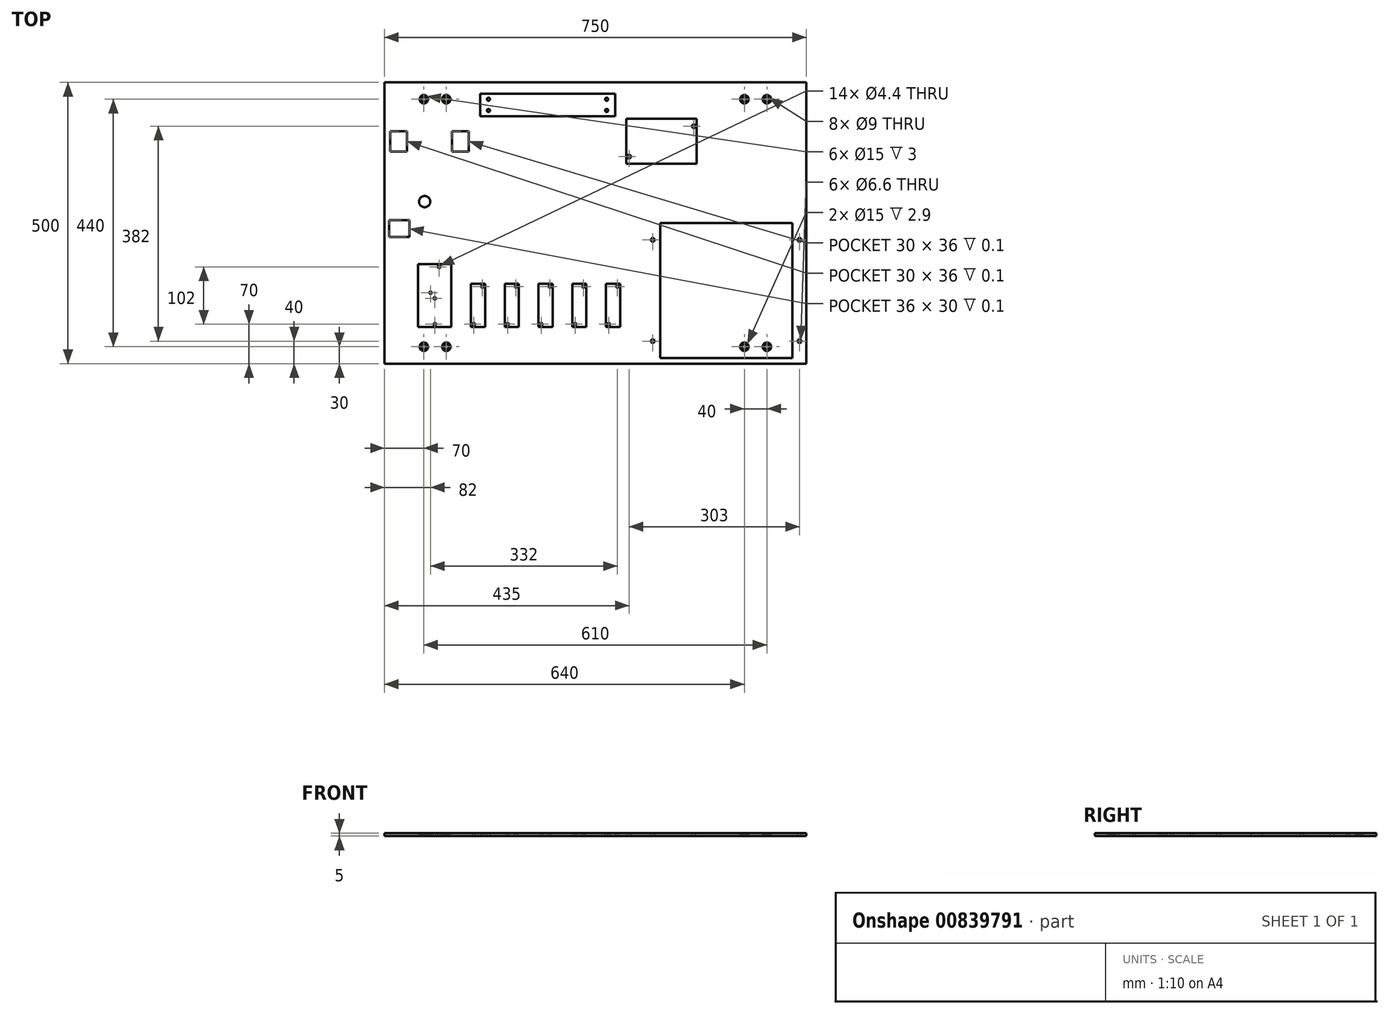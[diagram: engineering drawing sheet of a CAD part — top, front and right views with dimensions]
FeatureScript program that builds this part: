
annotation { "Feature Type Name" : "Feature", "Feature Type Description" : "" }
export const myFeature = defineFeature(function(context is Context, id is Id, definition is map)
    precondition{}
    {
        {
            var Q0;
            Q0=qCreatedBy(makeId("Top.planeOp"),FACE);
            var sketch = newSketch(context, id + "F0", { "sketchPlane" : qUnion([Q0])});
            skLineSegment(sketch, "E0.bottom", {"start": v(-375, 250) * mm, "end": v(375, 250) * mm});
            skLineSegment(sketch, "E0.top", {"start": v(-375, -250) * mm, "end": v(375, -250) * mm});
            skLineSegment(sketch, "E0.left", {"start": v(-375, 250) * mm, "end": v(-375, -250) * mm});
            skLineSegment(sketch, "E0.right", {"start": v(375, 250) * mm, "end": v(375, -250) * mm});
            skPoint(sketch, "E0.middle", {"position": v(0, 0) * mm});
            skSolve(sketch);
        }
        {
            var Q0;
            Q0=makeQuery(id+"F0.imprint","IMPRINT",FACE,{"disambiguationData":[TD([[makeQuery(id+"F0.imprint","IMPRINT",EDGE,{"derivedFrom":sQuery(id+"F0.wireOp",EDGE,"4meduJy7-bVkd-hp0T-bakh-5B8NUv365NF5")}),1.0]])]});
            var Q1;
            Q1=makeQuery(id+"F0.imprint","IMPRINT",FACE,{"disambiguationData":[TD([[makeQuery(id+"F0.imprint","IMPRINT",EDGE,{"derivedFrom":sQuery(id+"F0.wireOp",EDGE,"E0.bottom")}),-1.0]])]});
            var Q2;
            Q2=makeQuery(id+"F0.imprint","IMPRINT",FACE,{"disambiguationData":[TD([[makeQuery(id+"F0.imprint","IMPRINT",EDGE,{"derivedFrom":sQuery(id+"F0.wireOp",EDGE,"ac5e37f8-856c-49cc-b007-1c18f545f4330.MirrorC")}),-1.0]])]});
            var Q3;
            Q3=makeQuery(id+"F0.imprint","IMPRINT",FACE,{"disambiguationData":[TD([[makeQuery(id+"F0.imprint","IMPRINT",EDGE,{"derivedFrom":sQuery(id+"F0.wireOp",EDGE,"55b44df1-bd7d-4fb0-bc28-21b46cb8f5820.MirrorC")}),1.0]])]});
            var Q4;
            Q4=makeQuery(id+"F0.imprint","IMPRINT",FACE,{"disambiguationData":[TD([[makeQuery(id+"F0.imprint","IMPRINT",EDGE,{"derivedFrom":sQuery(id+"F0.wireOp",EDGE,"ec86db50-ea34-4b74-b64d-a008dce2ac710.MirrorC")}),-1.0]])]});
            var Q5;
            Q5=makeQuery(id+"F0.imprint","IMPRINT",FACE,{"disambiguationData":[TD([[makeQuery(id+"F0.imprint","IMPRINT",EDGE,{"derivedFrom":sQuery(id+"F0.wireOp",EDGE,"bd3b83fc-f496-4a5d-aeb5-383bc6339bfd0.MirrorC")}),1.0]])]});
            var Q6;
            Q6=makeQuery(id+"F0.imprint","IMPRINT",FACE,{"disambiguationData":[TD([[makeQuery(id+"F0.imprint","IMPRINT",EDGE,{"derivedFrom":sQuery(id+"F0.wireOp",EDGE,"f239e742-8900-48a1-b46c-c08f9f2a8f400.MirrorC")}),-1.0]])]});
            var Q7;
            Q7=makeQuery(id+"F0.imprint","IMPRINT",FACE,{"disambiguationData":[TD([[makeQuery(id+"F0.imprint","IMPRINT",EDGE,{"derivedFrom":sQuery(id+"F0.wireOp",EDGE,"240437df-a570-4469-8774-de0f0eec39ff0.MirrorC")}),-1.0]])]});
            var Q8;
            Q8=makeQuery(id+"F0.imprint","IMPRINT",FACE,{"disambiguationData":[TD([[makeQuery(id+"F0.imprint","IMPRINT",EDGE,{"derivedFrom":sQuery(id+"F0.wireOp",EDGE,"720a3da4-655f-46b3-9474-92b0fe536cc30.MirrorC")}),1.0]])]});
            extrude(context, id + "F1", {"entities" : qUnion([Q0, Q1, Q2, Q3, Q4, Q5, Q6, Q7, Q8]), "depth" : 5 * mm, "offsetDistance" : 25 * mm});
        }
        {
            var Q0;
            Q0=makeQuery(id+"F1.opExtrude","CAP_FACE",FACE,{"disambiguationData":[OSD([sQuery(id+"F0.wireOp",EDGE,"E0.bottom"),sQuery(id+"F0.wireOp",EDGE,"E0.top"),sQuery(id+"F0.wireOp",EDGE,"E0.left"),sQuery(id+"F0.wireOp",EDGE,"E0.right")])],"isStart":false});
            var sketch = newSketch(context, id + "F2", { "sketchPlane" : qUnion([Q0])});
            skPoint(sketch, "E1", {"position": v(-305, 220) * mm});
            skPoint(sketch, "E2", {"position": v(-265, 220) * mm});
            skPoint(sketch, "E3", {"position": v(265, 220) * mm});
            skPoint(sketch, "E4", {"position": v(305, 220) * mm});
            skPoint(sketch, "E5", {"position": v(-305, -220) * mm});
            skPoint(sketch, "E6", {"position": v(-265, -220) * mm});
            skPoint(sketch, "E7", {"position": v(265, -220) * mm});
            skPoint(sketch, "E8", {"position": v(305, -220) * mm});
            skSolve(sketch);
        }
        {
            var Q0;
            Q0=makeQuery(id+"F1.opExtrude","CAP_FACE",FACE,{"disambiguationData":[OSD([sQuery(id+"F0.wireOp",EDGE,"E0.bottom"),sQuery(id+"F0.wireOp",EDGE,"E0.top"),sQuery(id+"F0.wireOp",EDGE,"E0.left"),sQuery(id+"F0.wireOp",EDGE,"E0.right")])],"isStart":false});
            var sketch = newSketch(context, id + "F3", { "sketchPlane" : qUnion([Q0])});
            skLineSegment(sketch, "E9.bottom", {"start": v(115, 0) * mm, "end": v(350, 0) * mm});
            skLineSegment(sketch, "E9.top", {"start": v(115, -240) * mm, "end": v(350, -240) * mm});
            skLineSegment(sketch, "E9.left", {"start": v(115, 0) * mm, "end": v(115, -240) * mm});
            skLineSegment(sketch, "E9.right", {"start": v(350, 0) * mm, "end": v(350, -240) * mm});
            skLineSegment(sketch, "E10.bottom", {"start": v(-256, -185) * mm, "end": v(-315, -185) * mm});
            skLineSegment(sketch, "E10.top", {"start": v(-256, -73) * mm, "end": v(-315, -73) * mm});
            skLineSegment(sketch, "E10.left", {"start": v(-256, -185) * mm, "end": v(-256, -73) * mm});
            skLineSegment(sketch, "E10.right", {"start": v(-315, -185) * mm, "end": v(-315, -73) * mm});
            skLineSegment(sketch, "E11.bottom", {"start": v(-16, -108) * mm, "end": v(-41, -108) * mm});
            skLineSegment(sketch, "E11.top", {"start": v(-16, -185) * mm, "end": v(-41, -185) * mm});
            skLineSegment(sketch, "E11.left", {"start": v(-16, -108) * mm, "end": v(-16, -185) * mm});
            skLineSegment(sketch, "E11.right", {"start": v(-41, -108) * mm, "end": v(-41, -185) * mm});
            skLineSegment(sketch, "E12.bottom", {"start": v(-76, -108) * mm, "end": v(-101, -108) * mm});
            skLineSegment(sketch, "E12.top", {"start": v(-76, -185) * mm, "end": v(-101, -185) * mm});
            skLineSegment(sketch, "E12.left", {"start": v(-76, -108) * mm, "end": v(-76, -185) * mm});
            skLineSegment(sketch, "E12.right", {"start": v(-101, -108) * mm, "end": v(-101, -185) * mm});
            skLineSegment(sketch, "E13.bottom", {"start": v(-136, -108) * mm, "end": v(-161, -108) * mm});
            skLineSegment(sketch, "E13.top", {"start": v(-136, -185) * mm, "end": v(-161, -185) * mm});
            skLineSegment(sketch, "E13.left", {"start": v(-136, -108) * mm, "end": v(-136, -185) * mm});
            skLineSegment(sketch, "E13.right", {"start": v(-161, -108) * mm, "end": v(-161, -185) * mm});
            skLineSegment(sketch, "E14.bottom", {"start": v(-221, -108) * mm, "end": v(-196, -108) * mm});
            skLineSegment(sketch, "E14.top", {"start": v(-221, -185) * mm, "end": v(-196, -185) * mm});
            skLineSegment(sketch, "E14.left", {"start": v(-221, -108) * mm, "end": v(-221, -185) * mm});
            skLineSegment(sketch, "E14.right", {"start": v(-196, -108) * mm, "end": v(-196, -185) * mm});
            skLineSegment(sketch, "E15", {"start": v(-285, -50) * mm, "end": v(-285, 100) * mm});
            skLineSegment(sketch, "E16", {"start": v(-285, 100) * mm, "end": v(32, 100) * mm});
            skLineSegment(sketch, "E17.bottom", {"start": v(-205, 230) * mm, "end": v(35, 230) * mm});
            skLineSegment(sketch, "E17.top", {"start": v(-205, 190) * mm, "end": v(35, 190) * mm});
            skLineSegment(sketch, "E17.left", {"start": v(-205, 230) * mm, "end": v(-205, 190) * mm});
            skLineSegment(sketch, "E17.right", {"start": v(35, 230) * mm, "end": v(35, 190) * mm});
            skLineSegment(sketch, "E18.bottom", {"start": v(-324.13, 116.04) * mm, "end": v(-266.88, 116.04) * mm});
            skLineSegment(sketch, "E18.top", {"start": v(-324.13, 173.96) * mm, "end": v(-266.88, 173.96) * mm});
            skLineSegment(sketch, "E18.left", {"start": v(-324.13, 173.96) * mm, "end": v(-324.13, 116.04) * mm});
            skLineSegment(sketch, "E18.right", {"start": v(-266.88, 173.96) * mm, "end": v(-266.88, 116.04) * mm});
            skLineSegment(sketch, "E19", {"start": v(195, 210) * mm, "end": v(35, 210) * mm});
            skLineSegment(sketch, "E20", {"start": v(195, 210) * mm, "end": v(195, 165) * mm});
            skLineSegment(sketch, "E21", {"start": v(55, 145) * mm, "end": v(-266.88, 145) * mm});
            skPoint(sketch, "E22.1.internal.snap0", {"position": v(-285.5, -73) * mm});
            skPoint(sketch, "E23.2.internal.snap0", {"position": v(-208.5, -108) * mm});
            skPoint(sketch, "E24.1.internal.snap0", {"position": v(-148.5, -108) * mm});
            skLineSegment(sketch, "E25", {"start": v(-324.13, 145) * mm, "end": v(-363.07, 145) * mm});
            skLineSegment(sketch, "E26.bottom", {"start": v(55, 185) * mm, "end": v(180, 185) * mm});
            skLineSegment(sketch, "E26.top", {"start": v(55, 105) * mm, "end": v(180, 105) * mm});
            skLineSegment(sketch, "E26.left", {"start": v(55, 185) * mm, "end": v(55, 105) * mm});
            skLineSegment(sketch, "E26.right", {"start": v(180, 185) * mm, "end": v(180, 105) * mm});
            skPoint(sketch, "E27", {"position": v(55, 145) * mm});
            skLineSegment(sketch, "E28.left", {"start": v(210, 165) * mm, "end": v(210, 122.2) * mm});
            skPoint(sketch, "E28.middle", {"position": v(180, 145) * mm});
            skLineSegment(sketch, "E29", {"start": v(210, 122.2) * mm, "end": v(180, 122.2) * mm});
            skLineSegment(sketch, "E30", {"start": v(210, 165) * mm, "end": v(180, 165) * mm});
            skLineSegment(sketch, "E31", {"start": v(210, 143.6) * mm, "end": v(375, 143.6) * mm});
            skPoint(sketch, "E32", {"position": v(195, 165) * mm});
            skPoint(sketch, "E33", {"position": v(195, 122.2) * mm});
            skLineSegment(sketch, "E34", {"start": v(195, 100) * mm, "end": v(195, 122.2) * mm});
            skLineSegment(sketch, "E35", {"start": v(195, 30.37) * mm, "end": v(195, 100) * mm});
            skPoint(sketch, "E36", {"position": v(-295.5, 116.04) * mm});
            skLineSegment(sketch, "E37", {"start": v(-285, 100) * mm, "end": v(-295.5, 100) * mm});
            skLineSegment(sketch, "E38", {"start": v(-295.5, 100) * mm, "end": v(-295.5, 116.04) * mm});
            skLineSegment(sketch, "E39.bottom", {"start": v(19, -108) * mm, "end": v(44, -108) * mm});
            skLineSegment(sketch, "E39.top", {"start": v(19, -185) * mm, "end": v(44, -185) * mm});
            skLineSegment(sketch, "E39.left", {"start": v(19, -108) * mm, "end": v(19, -185) * mm});
            skLineSegment(sketch, "E39.right", {"start": v(44, -108) * mm, "end": v(44, -185) * mm});
            skLineSegment(sketch, "E40", {"start": v(-208.5, -108) * mm, "end": v(-208.5, -48) * mm});
            skLineSegment(sketch, "E41", {"start": v(-148.5, -108) * mm, "end": v(-148.5, 11.13) * mm});
            skLineSegment(sketch, "E42", {"start": v(-88.5, -108) * mm, "end": v(-88.5, 9.17) * mm});
            skLineSegment(sketch, "E43", {"start": v(-28.5, -108) * mm, "end": v(-28.5, -46.89) * mm});
            skLineSegment(sketch, "E44", {"start": v(31.5, -108) * mm, "end": v(31.5, 13.08) * mm});
            skSolve(sketch);
        }
        {
            var Q0;
            Q0=sQuery(id+"F2.wireOp",VERTEX,"E1");
            var Q1;
            Q1=sQuery(id+"F2.wireOp",VERTEX,"E2");
            var Q2;
            Q2=sQuery(id+"F2.wireOp",VERTEX,"E5");
            var Q3;
            Q3=sQuery(id+"F2.wireOp",VERTEX,"E6");
            var Q4;
            Q4=sQuery(id+"F2.wireOp",VERTEX,"E7");
            var Q5;
            Q5=sQuery(id+"F2.wireOp",VERTEX,"E8");
            var Q6;
            Q6=sQuery(id+"F2.wireOp",VERTEX,"E3");
            var Q7;
            Q7=sQuery(id+"F2.wireOp",VERTEX,"E4");
            var Q8;
            Q8=makeQuery(id+"F1.opExtrude","SWEPT_BODY",BODY,{"disambiguationData":[OSD([sQuery(id+"F0.wireOp",EDGE,"E0.bottom"),sQuery(id+"F0.wireOp",EDGE,"E0.top"),sQuery(id+"F0.wireOp",EDGE,"E0.left"),sQuery(id+"F0.wireOp",EDGE,"E0.right")])]});
            hole(context, id + "F4", {"style" : HoleStyle.C_BORE, "endStyle" : HoleEndStyle.THROUGH, "holeDiameter" : 9 * mm, "cBoreDiameter" : 15 * mm, "cBoreDepth" : 3 * mm, "majorDiameter" : 5 * mm, "isTappedThrough" : true, "tappedDepth" : 12 * mm, "tapClearance" : 3, "locations" : qUnion([Q0, Q1, Q2, Q3, Q4, Q5, Q6, Q7]), "scope" : qUnion([Q8])});
        }
        {
            var Q0;
            Q0=makeQuery(id+"F3.imprint","IMPRINT",FACE,{"disambiguationData":[TD([[makeQuery(id+"F3.imprint","IMPRINT",EDGE,{"derivedFrom":sQuery(id+"F3.wireOp",EDGE,"E9.bottom")}),-1.0]])]});
            extrude(context, id + "F5", {"entities" : qUnion([Q0]), "operationType" : NewBodyOperationType.REMOVE, "oppositeDirection" : true, "depth" : 0.1 * mm, "offsetDistance" : 25 * mm});
        }
        {
            var Q0;
            {var subQ3=sQuery(id+"F3.wireOp",EDGE,"E26.bottom");Q0=makeQuery(id+"F3.imprint","IMPRINT",FACE,{"disambiguationData":[TD([[makeQuery(id+"F3.imprint","IMPRINT",EDGE,{"derivedFrom":subQ3}),-1.0]])]});}
            extrude(context, id + "F6", {"entities" : qUnion([Q0]), "operationType" : NewBodyOperationType.REMOVE, "oppositeDirection" : true, "depth" : 0.1 * mm, "offsetDistance" : 25 * mm});
        }
        {
            var Q0;
            Q0=makeQuery(id+"F3.imprint","IMPRINT",FACE,{"disambiguationData":[TD([[makeQuery(id+"F3.imprint","IMPRINT",EDGE,{"derivedFrom":sQuery(id+"F3.wireOp",EDGE,"E10.bottom")}),-1.0]])]});
            extrude(context, id + "F7", {"entities" : qUnion([Q0]), "operationType" : NewBodyOperationType.REMOVE, "oppositeDirection" : true, "depth" : 0.1 * mm, "offsetDistance" : 25 * mm});
        }
        {
            var Q0;
            {var subQ1=sQuery(id+"F3.wireOp",EDGE,"E17.bottom");Q0=makeQuery(id+"F3.imprint","IMPRINT",FACE,{"disambiguationData":[TD([[makeQuery(id+"F3.imprint","IMPRINT",EDGE,{"derivedFrom":subQ1}),-1.0]])]});}
            extrude(context, id + "F8", {"entities" : qUnion([Q0]), "operationType" : NewBodyOperationType.REMOVE, "oppositeDirection" : true, "depth" : 0.1 * mm, "offsetDistance" : 25 * mm});
        }
        {
            var Q0;
            Q0=makeQuery(id+"F3.imprint","IMPRINT",FACE,{"disambiguationData":[TD([[makeQuery(id+"F3.imprint","IMPRINT",EDGE,{"derivedFrom":sQuery(id+"F3.wireOp",EDGE,"E14.top")}),1.0]])]});
            var Q1;
            Q1=makeQuery(id+"F3.imprint","IMPRINT",FACE,{"disambiguationData":[TD([[makeQuery(id+"F3.imprint","IMPRINT",EDGE,{"derivedFrom":sQuery(id+"F3.wireOp",EDGE,"E13.top")}),-1.0]])]});
            var Q2;
            Q2=makeQuery(id+"F3.imprint","IMPRINT",FACE,{"disambiguationData":[TD([[makeQuery(id+"F3.imprint","IMPRINT",EDGE,{"derivedFrom":sQuery(id+"F3.wireOp",EDGE,"E12.top")}),-1.0]])]});
            var Q3;
            Q3=makeQuery(id+"F3.imprint","IMPRINT",FACE,{"disambiguationData":[TD([[makeQuery(id+"F3.imprint","IMPRINT",EDGE,{"derivedFrom":sQuery(id+"F3.wireOp",EDGE,"E11.top")}),-1.0]])]});
            var Q4;
            Q4=makeQuery(id+"F3.imprint","IMPRINT",FACE,{"disambiguationData":[TD([[makeQuery(id+"F3.imprint","IMPRINT",EDGE,{"derivedFrom":sQuery(id+"F3.wireOp",EDGE,"E39.bottom")}),-1.0]])]});
            extrude(context, id + "F9", {"entities" : qUnion([Q0, Q1, Q2, Q3, Q4]), "operationType" : NewBodyOperationType.REMOVE, "oppositeDirection" : true, "depth" : 0.1 * mm, "offsetDistance" : 25 * mm});
        }
        {
            var Q0;
            Q0=makeQuery(id+"F1.opExtrude","CAP_FACE",FACE,{"disambiguationData":[OSD([sQuery(id+"F0.wireOp",EDGE,"E0.bottom"),sQuery(id+"F0.wireOp",EDGE,"E0.top"),sQuery(id+"F0.wireOp",EDGE,"E0.left"),sQuery(id+"F0.wireOp",EDGE,"E0.right")])],"isStart":false});
            var sketch = newSketch(context, id + "F10", { "sketchPlane" : qUnion([Q0])});
            skPoint(sketch, "E45", {"position": v(-201, -113) * mm});
            skPoint(sketch, "E46", {"position": v(-216, -180) * mm});
            skPoint(sketch, "E47", {"position": v(-278, -78) * mm});
            skPoint(sketch, "E48", {"position": v(-293, -124) * mm});
            skPoint(sketch, "E49", {"position": v(-285.5, -134) * mm});
            skPoint(sketch, "E50", {"position": v(-285.5, -180) * mm});
            skPoint(sketch, "E51", {"position": v(-141, -113) * mm});
            skPoint(sketch, "E52", {"position": v(-156, -180) * mm});
            skPoint(sketch, "E53", {"position": v(-96, -180) * mm});
            skPoint(sketch, "E54", {"position": v(-81, -113) * mm});
            skPoint(sketch, "E55", {"position": v(-21, -113) * mm});
            skPoint(sketch, "E56", {"position": v(-36, -180) * mm});
            skPoint(sketch, "E57", {"position": v(24, -180) * mm});
            skPoint(sketch, "E58", {"position": v(39, -113) * mm});
            skPoint(sketch, "E59", {"position": v(-190, 220) * mm});
            skLineSegment(sketch, "E60", {"start": v(-205, 210) * mm, "end": v(35, 210) * mm, "construction": true});
            skLineSegment(sketch, "E61", {"start": v(-85, 190) * mm, "end": v(-85, 230) * mm, "construction": true});
            skPoint(sketch, "E62.MirrorP", {"position": v(-190, 200) * mm});
            skPoint(sketch, "E63.MirrorP", {"position": v(20, 220) * mm});
            skPoint(sketch, "E64.MirrorP", {"position": v(20, 200) * mm});
            skPoint(sketch, "E65", {"position": v(60, 118) * mm});
            skPoint(sketch, "E66", {"position": v(175, 172) * mm});
            skPoint(sketch, "E67", {"position": v(102, -30) * mm});
            skLineSegment(sketch, "E68", {"start": v(232.5, 0) * mm, "end": v(232.5, -240) * mm, "construction": true});
            skLineSegment(sketch, "E69", {"start": v(115, -120) * mm, "end": v(350, -120) * mm, "construction": true});
            skPoint(sketch, "E70.MirrorP", {"position": v(363, -30) * mm});
            skPoint(sketch, "E71.MirrorP", {"position": v(102, -210) * mm});
            skPoint(sketch, "E72.MirrorP", {"position": v(363, -210) * mm});
            skSolve(sketch);
        }
        {
            var Q0;
            Q0=sQuery(id+"F10.wireOp",VERTEX,"E49");
            var Q1;
            Q1=sQuery(id+"F10.wireOp",VERTEX,"E48");
            var Q2;
            Q2=sQuery(id+"F10.wireOp",VERTEX,"E47");
            var Q3;
            Q3=sQuery(id+"F10.wireOp",VERTEX,"E50");
            var Q4;
            Q4=sQuery(id+"F10.wireOp",VERTEX,"E46");
            var Q5;
            Q5=sQuery(id+"F10.wireOp",VERTEX,"E45");
            var Q6;
            Q6=sQuery(id+"F10.wireOp",VERTEX,"E51");
            var Q7;
            Q7=sQuery(id+"F10.wireOp",VERTEX,"E52");
            var Q8;
            Q8=sQuery(id+"F10.wireOp",VERTEX,"E53");
            var Q9;
            Q9=sQuery(id+"F10.wireOp",VERTEX,"E54");
            var Q10;
            Q10=sQuery(id+"F10.wireOp",VERTEX,"E55");
            var Q11;
            Q11=sQuery(id+"F10.wireOp",VERTEX,"E56");
            var Q12;
            Q12=sQuery(id+"F10.wireOp",VERTEX,"E57");
            var Q13;
            Q13=sQuery(id+"F10.wireOp",VERTEX,"E58");
            var Q14;
            Q14=makeQuery(id+"F1.opExtrude","SWEPT_BODY",BODY,{"disambiguationData":[OSD([sQuery(id+"F0.wireOp",EDGE,"E0.bottom"),sQuery(id+"F0.wireOp",EDGE,"E0.top"),sQuery(id+"F0.wireOp",EDGE,"E0.left"),sQuery(id+"F0.wireOp",EDGE,"E0.right")])]});
            hole(context, id + "F11", {"style" : HoleStyle.SIMPLE, "endStyle" : HoleEndStyle.THROUGH, "standardTappedOrClearance" : lookupTablePath({ "fit" : "Normal", "standard" : "ISO", "size" : "M4", "type" : "Clearance" }), "standardBlindInLast" : lookupTablePath({ "fit" : "Standard", "standard" : "ISO", "size" : "M4", "type" : "Clearance" }), "holeDiameter" : 4.4 * mm, "majorDiameter" : 5 * mm, "isTappedThrough" : true, "tappedDepth" : 12 * mm, "tapClearance" : 3, "locations" : qUnion([Q0, Q1, Q2, Q3, Q4, Q5, Q6, Q7, Q8, Q9, Q10, Q11, Q12, Q13]), "scope" : qUnion([Q14])});
        }
        {
            var Q0;
            Q0=sQuery(id+"F10.wireOp",VERTEX,"E59");
            var Q1;
            Q1=sQuery(id+"F10.wireOp",VERTEX,"E62.MirrorP");
            var Q2;
            Q2=sQuery(id+"F10.wireOp",VERTEX,"E64.MirrorP");
            var Q3;
            Q3=sQuery(id+"F10.wireOp",VERTEX,"E63.MirrorP");
            var Q4;
            Q4=makeQuery(id+"F1.opExtrude","SWEPT_BODY",BODY,{"disambiguationData":[OSD([sQuery(id+"F0.wireOp",EDGE,"E0.bottom"),sQuery(id+"F0.wireOp",EDGE,"E0.top"),sQuery(id+"F0.wireOp",EDGE,"E0.left"),sQuery(id+"F0.wireOp",EDGE,"E0.right")])]});
            hole(context, id + "F12", {"style" : HoleStyle.SIMPLE, "endStyle" : HoleEndStyle.THROUGH, "standardTappedOrClearance" : lookupTablePath({ "fit" : "Normal", "standard" : "ISO", "size" : "M5", "type" : "Clearance" }), "standardBlindInLast" : lookupTablePath({ "fit" : "Standard", "standard" : "ISO", "size" : "M5", "type" : "Clearance" }), "holeDiameter" : 5.5 * mm, "majorDiameter" : 5 * mm, "isTappedThrough" : true, "tappedDepth" : 12 * mm, "tapClearance" : 3, "locations" : qUnion([Q0, Q1, Q2, Q3]), "scope" : qUnion([Q4])});
        }
        {
            var Q0;
            Q0=sQuery(id+"F10.wireOp",VERTEX,"E65");
            var Q1;
            Q1=sQuery(id+"F10.wireOp",VERTEX,"E66");
            var Q2;
            Q2=sQuery(id+"F10.wireOp",VERTEX,"E67");
            var Q3;
            Q3=sQuery(id+"F10.wireOp",VERTEX,"E71.MirrorP");
            var Q4;
            Q4=sQuery(id+"F10.wireOp",VERTEX,"E72.MirrorP");
            var Q5;
            Q5=sQuery(id+"F10.wireOp",VERTEX,"E70.MirrorP");
            var Q6;
            Q6=makeQuery(id+"F1.opExtrude","SWEPT_BODY",BODY,{"disambiguationData":[OSD([sQuery(id+"F0.wireOp",EDGE,"E0.bottom"),sQuery(id+"F0.wireOp",EDGE,"E0.top"),sQuery(id+"F0.wireOp",EDGE,"E0.left"),sQuery(id+"F0.wireOp",EDGE,"E0.right")])]});
            hole(context, id + "F13", {"style" : HoleStyle.SIMPLE, "endStyle" : HoleEndStyle.THROUGH, "standardTappedOrClearance" : lookupTablePath({ "fit" : "Normal", "standard" : "ISO", "size" : "M6", "type" : "Clearance" }), "standardBlindInLast" : lookupTablePath({ "fit" : "Standard", "standard" : "ISO", "size" : "M6", "type" : "Clearance" }), "holeDiameter" : 6.6 * mm, "majorDiameter" : 5 * mm, "isTappedThrough" : true, "tappedDepth" : 12 * mm, "tapClearance" : 3, "locations" : qUnion([Q0, Q1, Q2, Q3, Q4, Q5]), "scope" : qUnion([Q6])});
        }
        {
            var Q0;
            Q0=makeQuery(id+"F1.opExtrude","CAP_FACE",FACE,{"disambiguationData":[OSD([sQuery(id+"F0.wireOp",EDGE,"E0.bottom"),sQuery(id+"F0.wireOp",EDGE,"E0.top"),sQuery(id+"F0.wireOp",EDGE,"E0.left"),sQuery(id+"F0.wireOp",EDGE,"E0.right")])],"isStart":false});
            var sketch = newSketch(context, id + "F14", { "sketchPlane" : qUnion([Q0])});
            skPoint(sketch, "E73", {"position": v(-303.5, 38) * mm});
            skSolve(sketch);
        }
        {
            var Q0;
            Q0=sQuery(id+"F14.wireOp",VERTEX,"E73");
            var Q1;
            Q1=makeQuery(id+"F1.opExtrude","SWEPT_BODY",BODY,{"disambiguationData":[OSD([sQuery(id+"F0.wireOp",EDGE,"E0.bottom"),sQuery(id+"F0.wireOp",EDGE,"E0.top"),sQuery(id+"F0.wireOp",EDGE,"E0.left"),sQuery(id+"F0.wireOp",EDGE,"E0.right")])]});
            hole(context, id + "F15", {"style" : HoleStyle.SIMPLE, "endStyle" : HoleEndStyle.THROUGH, "holeDiameter" : 20 * mm, "majorDiameter" : 5 * mm, "isTappedThrough" : true, "tappedDepth" : 12 * mm, "tapClearance" : 3, "locations" : qUnion([Q0]), "scope" : qUnion([Q1])});
        }
        {
            var Q0;
            Q0=makeQuery(id+"F1.opExtrude","CAP_FACE",FACE,{"disambiguationData":[OSD([sQuery(id+"F0.wireOp",EDGE,"E0.bottom"),sQuery(id+"F0.wireOp",EDGE,"E0.top"),sQuery(id+"F0.wireOp",EDGE,"E0.left"),sQuery(id+"F0.wireOp",EDGE,"E0.right")])],"isStart":false});
            var sketch = newSketch(context, id + "F16", { "sketchPlane" : qUnion([Q0])});
            skLineSegment(sketch, "E74.bottom", {"start": v(-366.5, 5) * mm, "end": v(-330.5, 5) * mm});
            skLineSegment(sketch, "E74.top", {"start": v(-366.5, -25) * mm, "end": v(-330.5, -25) * mm});
            skLineSegment(sketch, "E74.left", {"start": v(-366.5, 5) * mm, "end": v(-366.5, -25) * mm});
            skLineSegment(sketch, "E74.right", {"start": v(-330.5, 5) * mm, "end": v(-330.5, -25) * mm});
            skPoint(sketch, "E74.middle", {"position": v(-348.5, -10) * mm});
            skLineSegment(sketch, "E75", {"start": v(55, 145) * mm, "end": v(-402.73, 145) * mm, "construction": true});
            skLineSegment(sketch, "E76.bottom", {"start": v(-255, 163) * mm, "end": v(-225, 163) * mm});
            skLineSegment(sketch, "E76.top", {"start": v(-255, 127) * mm, "end": v(-225, 127) * mm});
            skLineSegment(sketch, "E76.left", {"start": v(-255, 163) * mm, "end": v(-255, 127) * mm});
            skLineSegment(sketch, "E76.right", {"start": v(-225, 163) * mm, "end": v(-225, 127) * mm});
            skPoint(sketch, "E76.middle", {"position": v(-240, 145) * mm});
            skLineSegment(sketch, "E77.bottom", {"start": v(-365, 163) * mm, "end": v(-335, 163) * mm});
            skLineSegment(sketch, "E77.top", {"start": v(-365, 127) * mm, "end": v(-335, 127) * mm});
            skLineSegment(sketch, "E77.left", {"start": v(-365, 163) * mm, "end": v(-365, 127) * mm});
            skLineSegment(sketch, "E77.right", {"start": v(-335, 163) * mm, "end": v(-335, 127) * mm});
            skPoint(sketch, "E77.middle", {"position": v(-350, 145) * mm});
            skSolve(sketch);
        }
        {
            var Q0;
            Q0=makeQuery(id+"F16.imprint","IMPRINT",FACE,{"disambiguationData":[TD([[makeQuery(id+"F16.imprint","IMPRINT",EDGE,{"derivedFrom":sQuery(id+"F16.wireOp",EDGE,"E74.bottom")}),-1.0]])]});
            var Q1;
            Q1=makeQuery(id+"F16.imprint","IMPRINT",FACE,{"disambiguationData":[TD([[makeQuery(id+"F16.imprint","IMPRINT",EDGE,{"derivedFrom":sQuery(id+"F16.wireOp",EDGE,"E77.bottom")}),-1.0]])]});
            var Q2;
            Q2=makeQuery(id+"F16.imprint","IMPRINT",FACE,{"disambiguationData":[TD([[makeQuery(id+"F16.imprint","IMPRINT",EDGE,{"derivedFrom":sQuery(id+"F16.wireOp",EDGE,"E76.bottom")}),-1.0]])]});
            extrude(context, id + "F17", {"entities" : qUnion([Q0, Q1, Q2]), "operationType" : NewBodyOperationType.REMOVE, "oppositeDirection" : true, "depth" : 0.1 * mm, "offsetDistance" : 25 * mm});
        }
    });
